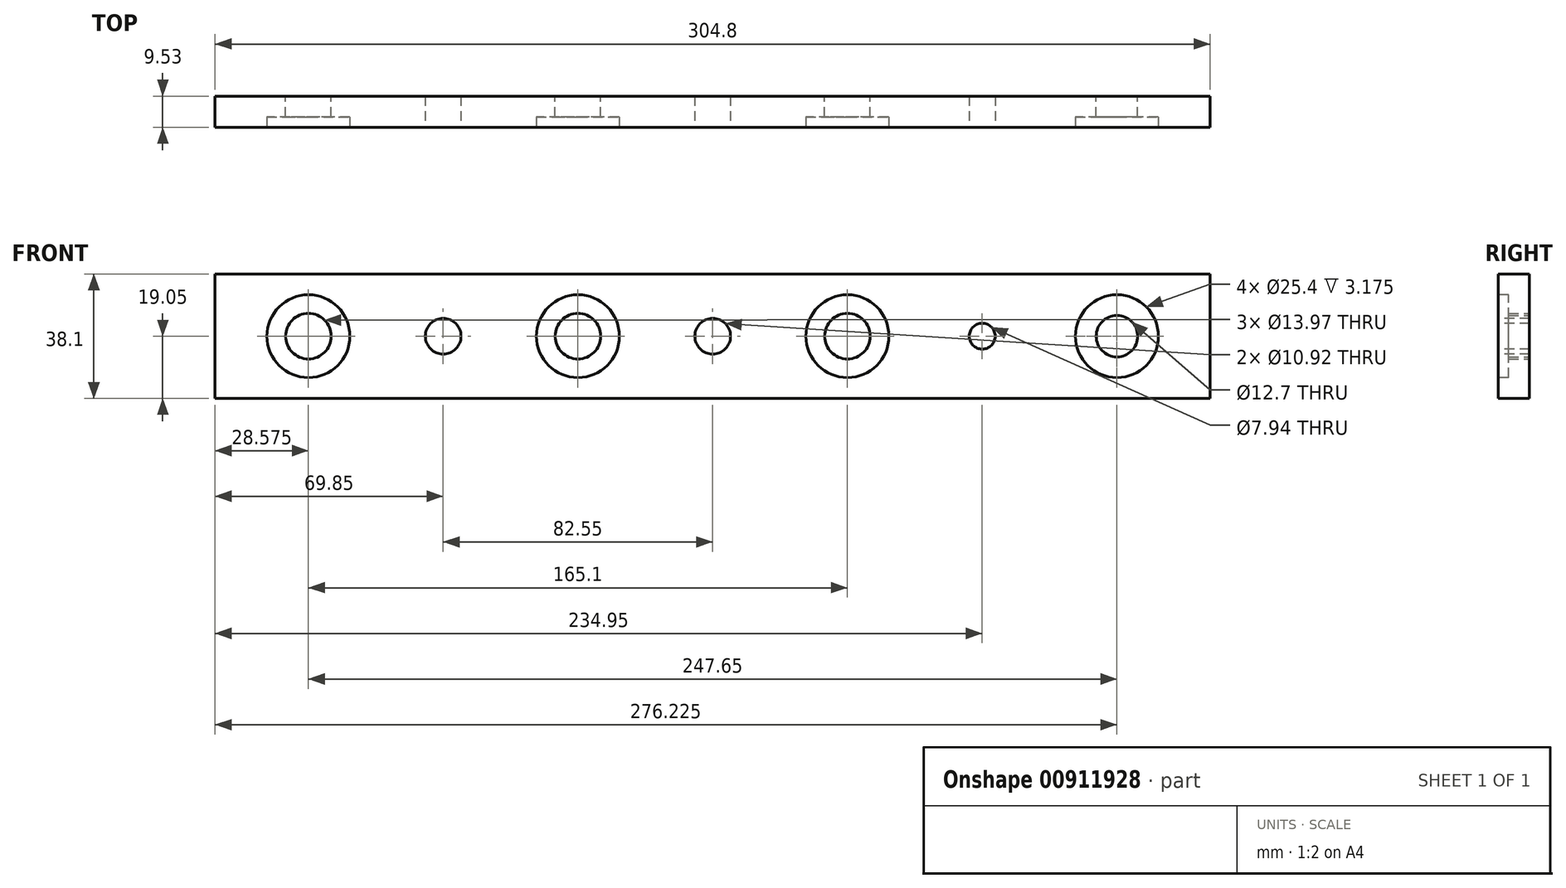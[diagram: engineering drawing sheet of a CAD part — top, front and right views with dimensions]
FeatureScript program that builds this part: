
annotation { "Feature Type Name" : "Feature", "Feature Type Description" : "" }
export const myFeature = defineFeature(function(context is Context, id is Id, definition is map)
    precondition{}
    {
        {
            var Q0;
            Q0=qCreatedBy(makeId("Front.planeOp"),FACE);
            var sketch = newSketch(context, id + "F0", { "sketchPlane" : qUnion([Q0])});
            skLineSegment(sketch, "E0.bottom", {"start": v(0, 0) * mm, "end": v(304.8, 0) * mm});
            skLineSegment(sketch, "E0.top", {"start": v(0, 38.1) * mm, "end": v(304.8, 38.1) * mm});
            skLineSegment(sketch, "E0.left", {"start": v(0, 0) * mm, "end": v(0, 38.1) * mm});
            skLineSegment(sketch, "E0.right", {"start": v(304.8, 0) * mm, "end": v(304.8, 38.1) * mm});
            skCircle(sketch, "E1", {"center": v(28.57, 19.05) * mm, "radius": 6.99 * mm});
            skCircle(sketch, "E2", {"center": v(111.12, 19.05) * mm, "radius": 6.99 * mm});
            skCircle(sketch, "E3", {"center": v(193.68, 19.05) * mm, "radius": 6.99 * mm});
            skCircle(sketch, "E4", {"center": v(276.23, 19.05) * mm, "radius": 6.35 * mm});
            skSolve(sketch);
        }
        {
            var Q0;
            Q0=makeQuery(id+"F0.imprint","IMPRINT",FACE,{"disambiguationData":[TD([[makeQuery(id+"F0.imprint","IMPRINT",EDGE,{"derivedFrom":sQuery(id+"F0.wireOp",EDGE,"E0.bottom")}),1.0]])]});
            extrude(context, id + "F1", {"entities" : qUnion([Q0]), "depth" : 9.52 * mm, "offsetDistance" : 25.4 * mm});
        }
        {
            var Q0;
            Q0=makeQuery(id+"F1.opExtrude","CAP_FACE",FACE,{"disambiguationData":[OSD([sQuery(id+"F0.wireOp",EDGE,"E0.bottom"),sQuery(id+"F0.wireOp",EDGE,"E0.top"),sQuery(id+"F0.wireOp",EDGE,"E0.left"),sQuery(id+"F0.wireOp",EDGE,"E0.right"),sQuery(id+"F0.wireOp",EDGE,"E1"),sQuery(id+"F0.wireOp",EDGE,"E2"),sQuery(id+"F0.wireOp",EDGE,"E3"),sQuery(id+"F0.wireOp",EDGE,"E4")])],"isStart":false});
            var sketch = newSketch(context, id + "F2", { "sketchPlane" : qUnion([Q0])});
            skCircle(sketch, "E5", {"center": v(69.85, 19.05) * mm, "radius": 5.46 * mm});
            skCircle(sketch, "E6", {"center": v(152.4, 19.05) * mm, "radius": 5.46 * mm});
            skCircle(sketch, "E7", {"center": v(234.95, 19.05) * mm, "radius": 3.97 * mm});
            skCircle(sketch, "E8", {"center": v(28.57, 19.05) * mm, "radius": 12.7 * mm});
            skCircle(sketch, "E9", {"center": v(111.12, 19.05) * mm, "radius": 12.7 * mm});
            skCircle(sketch, "E10", {"center": v(193.68, 19.05) * mm, "radius": 12.7 * mm});
            skCircle(sketch, "E11", {"center": v(276.23, 19.05) * mm, "radius": 12.7 * mm});
            skSolve(sketch);
        }
        {
            var Q0;
            Q0=makeQuery(id+"F2.imprint","IMPRINT",FACE,{"disambiguationData":[TD([[makeQuery(id+"F2.imprint","IMPRINT",EDGE,{"derivedFrom":sQuery(id+"F2.wireOp",EDGE,"E5")}),1.0]])]});
            var Q1;
            Q1=makeQuery(id+"F2.imprint","IMPRINT",FACE,{"disambiguationData":[TD([[makeQuery(id+"F2.imprint","IMPRINT",EDGE,{"derivedFrom":sQuery(id+"F2.wireOp",EDGE,"E6")}),1.0]])]});
            var Q2;
            Q2=makeQuery(id+"F2.imprint","IMPRINT",FACE,{"disambiguationData":[TD([[makeQuery(id+"F2.imprint","IMPRINT",EDGE,{"derivedFrom":sQuery(id+"F2.wireOp",EDGE,"E7")}),1.0]])]});
            extrude(context, id + "F3", {"entities" : qUnion([Q0, Q1, Q2]), "operationType" : NewBodyOperationType.REMOVE, "endBound" : BoundingType.THROUGH_ALL, "oppositeDirection" : true, "depth" : 25.4 * mm, "offsetDistance" : 25.4 * mm});
        }
        {
            var Q0;
            Q0=makeQuery(id+"F2.imprint","IMPRINT",FACE,{"disambiguationData":[TD([[makeQuery(id+"F2.imprint","IMPRINT",EDGE,{"derivedFrom":sQuery(id+"F2.wireOp",EDGE,"E8")}),1.0]])]});
            var Q1;
            Q1=makeQuery(id+"F2.imprint","IMPRINT",FACE,{"disambiguationData":[TD([[makeQuery(id+"F2.imprint","IMPRINT",EDGE,{"derivedFrom":sQuery(id+"F2.wireOp",EDGE,"E9")}),1.0]])]});
            var Q2;
            Q2=makeQuery(id+"F2.imprint","IMPRINT",FACE,{"disambiguationData":[TD([[makeQuery(id+"F2.imprint","IMPRINT",EDGE,{"derivedFrom":sQuery(id+"F2.wireOp",EDGE,"E10")}),1.0]])]});
            var Q3;
            Q3=makeQuery(id+"F2.imprint","IMPRINT",FACE,{"disambiguationData":[TD([[makeQuery(id+"F2.imprint","IMPRINT",EDGE,{"derivedFrom":sQuery(id+"F2.wireOp",EDGE,"E11")}),1.0]])]});
            extrude(context, id + "F4", {"entities" : qUnion([Q0, Q1, Q2, Q3]), "operationType" : NewBodyOperationType.REMOVE, "oppositeDirection" : true, "depth" : 3.17 * mm, "offsetDistance" : 25.4 * mm});
        }
    });
